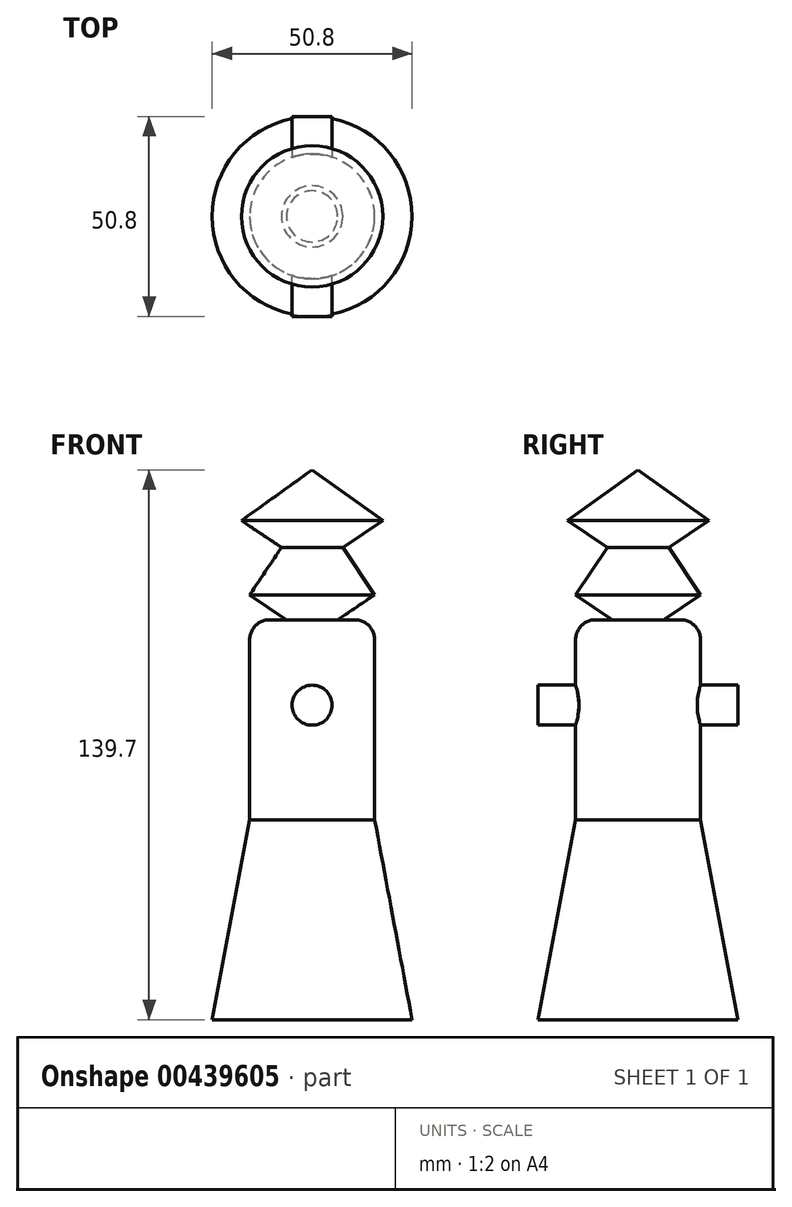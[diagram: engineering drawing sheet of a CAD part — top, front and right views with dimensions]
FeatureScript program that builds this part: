
annotation { "Feature Type Name" : "Feature", "Feature Type Description" : "" }
export const myFeature = defineFeature(function(context is Context, id is Id, definition is map)
    precondition{}
    {
        {
            var Q0;
            Q0=qCreatedBy(makeId("Top.planeOp"),FACE);
            var sketch = newSketch(context, id + "F0", { "sketchPlane" : qUnion([Q0])});
            skCircle(sketch, "E0", {"center": v(0, 0) * mm, "radius": 25.4 * mm});
            skSolve(sketch);
        }
        {
            var Q0;
            Q0=qCreatedBy(makeId("Top.planeOp"),FACE);
            cPlane(context, id + "F1", {"entities" : qUnion([Q0]), "cplaneType" : CPlaneType.OFFSET, "offset" : 50.8 * mm, "width" : 152.4 * mm, "height" : 152.4 * mm});
        }
        {
            var Q0;
            Q0=qCreatedBy(id+"F1.planeOp",FACE);
            var sketch = newSketch(context, id + "F2", { "sketchPlane" : qUnion([Q0])});
            skCircle(sketch, "E1", {"center": v(0, 0) * mm, "radius": 15.88 * mm});
            skSolve(sketch);
        }
        {
            var Q0;
            Q0=makeQuery(id+"F0.imprint","IMPRINT",FACE,{"disambiguationData":[TD([[makeQuery(id+"F0.imprint","IMPRINT",EDGE,{"derivedFrom":sQuery(id+"F0.wireOp",EDGE,"E0")}),1.0]])]});
            var Q1;
            Q1=makeQuery(id+"F2.imprint","IMPRINT",FACE,{"disambiguationData":[TD([[makeQuery(id+"F2.imprint","IMPRINT",EDGE,{"derivedFrom":sQuery(id+"F2.wireOp",EDGE,"E1")}),1.0]])]});
            loft(context, id + "F3", {"sheetProfilesArray" : [{ "sheetProfileEntities" : qUnion([Q0]) }, { "sheetProfileEntities" : qUnion([Q1]) }]});
        }
        {
            var Q0;
            Q0=makeQuery(id+"F3.opLoft","CAP_FACE",FACE,{"disambiguationData":[OSD([makeQuery(id+"F2.imprint","IMPRINT",FACE,{"disambiguationData":[TD([[makeQuery(id+"F2.imprint","IMPRINT",EDGE,{"derivedFrom":sQuery(id+"F2.wireOp",EDGE,"E1")}),1.0]])]})])],"isStart":true});
            var sketch = newSketch(context, id + "F4", { "sketchPlane" : qUnion([Q0])});
            skSolve(sketch);
        }
        {
            var Q0;
            Q0=makeQuery(id+"F4.imprint","IMPRINT",FACE,{"disambiguationData":[TD([[makeQuery(id+"F4.imprint","IMPRINT",EDGE,{"derivedFrom":makeQuery(id+"F3.opLoft","MID_CAP_EDGE",EDGE,{"disambiguationData":[OSD([sQuery(id+"F0.wireOp",EDGE,"E0"),sQuery(id+"F2.wireOp",EDGE,"E1")])],"capPos":1.0})}),1.0]])]});
            extrude(context, id + "F5", {"entities" : qUnion([Q0]), "operationType" : NewBodyOperationType.ADD, "depth" : 50.8 * mm});
        }
        {
            var Q0;
            Q0=qCreatedBy(makeId("Front.planeOp"),FACE);
            var sketch = newSketch(context, id + "F6", { "sketchPlane" : qUnion([Q0])});
            skCircle(sketch, "E2", {"center": v(0, 79.9) * mm, "radius": 5.08 * mm});
            skSolve(sketch);
        }
        {
            var Q0;
            Q0 = qSketchRegion(id + "F6", true);
            extrude(context, id + "F7", {"entities" : qUnion([Q0]), "operationType" : NewBodyOperationType.ADD, "depth" : 25.4 * mm});
        }
        {
            var Q0;
            Q0=makeQuery(id+"F7.opExtrude","CAP_FACE",FACE,{"disambiguationData":[OSD([sQuery(id+"F6.wireOp",EDGE,"E2")])],"isStart":false});
            extrude(context, id + "F8", {"entities" : qUnion([Q0]), "operationType" : NewBodyOperationType.ADD, "oppositeDirection" : true, "depth" : 50.8 * mm});
        }
        {
            var Q0;
            Q0=makeQuery(id+"F5.opExtrude","CAP_EDGE",EDGE,{"disambiguationData":[OSD([sQuery(id+"F0.wireOp",EDGE,"E0"),sQuery(id+"F2.wireOp",EDGE,"E1")])],"isStart":false});
            fillet(context, id + "F9", {"entities" : qUnion([Q0]), "radius" : 5.08 * mm, "tangentPropagation" : true, "allowEdgeOverflow" : false});
        }
        {
            var Q0;
            Q0=qCreatedBy(makeId("Front.planeOp"),FACE);
            var sketch = newSketch(context, id + "F10", { "sketchPlane" : qUnion([Q0])});
            skLineSegment(sketch, "E3", {"start": v(0, 0) * mm, "end": v(0, 139.7) * mm});
            skLineSegment(sketch, "E4", {"start": v(0, 139.7) * mm, "end": v(-17.94, 126.8) * mm});
            skLineSegment(sketch, "E5", {"start": v(-17.94, 126.8) * mm, "end": v(-7.78, 119.97) * mm});
            skLineSegment(sketch, "E6", {"start": v(-7.78, 119.97) * mm, "end": v(-15.88, 107.92) * mm});
            skLineSegment(sketch, "E7", {"start": v(-15.88, 107.92) * mm, "end": v(0, 97.24) * mm});
            skSolve(sketch);
        }
        {
            var Q0;
            {var subQ0=sQuery(id+"F10.wireOp",EDGE,"E4");Q0=makeQuery(id+"F10.imprint","IMPRINT",FACE,{"disambiguationData":[TD([[makeQuery(id+"F10.imprint","IMPRINT",EDGE,{"derivedFrom":subQ0}),1.0]])]});}
            var Q1;
            Q1=sQuery(id+"F10.wireOp",EDGE,"E3");
            revolve(context, id + "F11", {"operationType" : NewBodyOperationType.ADD, "entities" : qUnion([Q0]), "axis" : qUnion([Q1]), "revolveType" : RevolveType.FULL});
        }
    });
